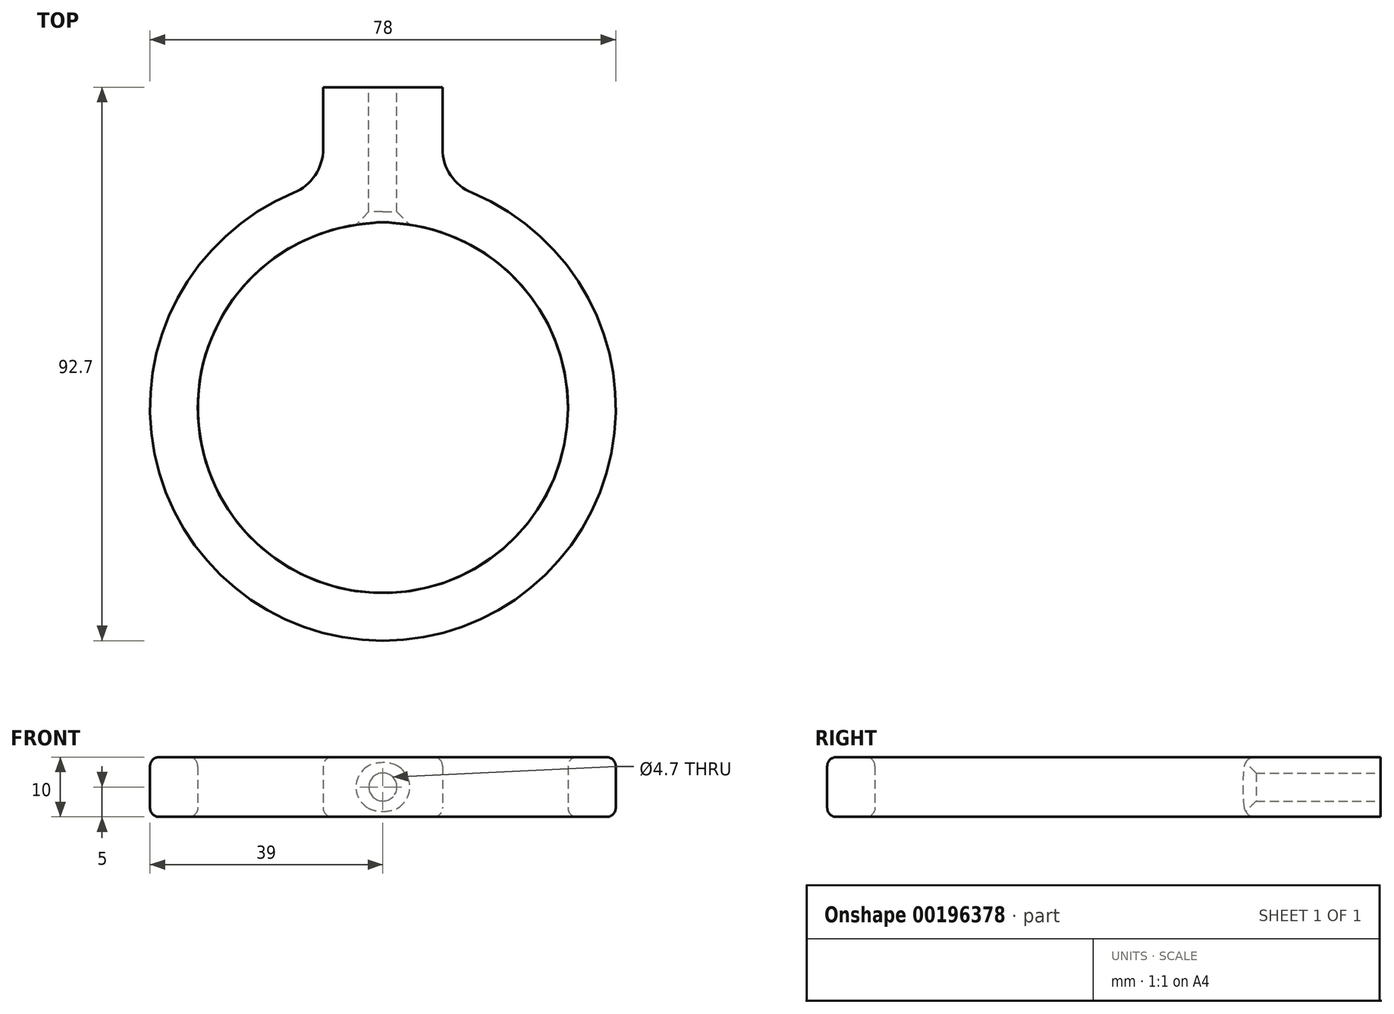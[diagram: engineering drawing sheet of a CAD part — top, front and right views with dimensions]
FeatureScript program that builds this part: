
annotation { "Feature Type Name" : "Feature", "Feature Type Description" : "" }
export const myFeature = defineFeature(function(context is Context, id is Id, definition is map)
    precondition{}
    {
        {
            var Q0;
            Q0=qCreatedBy(makeId("Top.planeOp"),FACE);
            var sketch = newSketch(context, id + "F0", { "sketchPlane" : qUnion([Q0])});
            skCircle(sketch, "E0", {"center": v(0, 0) * mm, "radius": 31 * mm});
            skArc(sketch, "E1.0", {"start": v(-14.94, 36.03) * mm, "mid": v(0, -39) * mm, "end": v(14.94, 36.03) * mm});
            skLineSegment(sketch, "E2.top", {"start": v(-10, 53.7) * mm, "end": v(10, 53.7) * mm});
            skLineSegment(sketch, "E2.left", {"start": v(-10, 43.42) * mm, "end": v(-10, 53.7) * mm});
            skLineSegment(sketch, "E2.right", {"start": v(10, 43.42) * mm, "end": v(10, 53.7) * mm});
            skPoint(sketch, "E2.middle", {"position": v(0, 45.7) * mm});
            skPoint(sketch, "E3.visualSharp", {"position": v(-10, 37.7) * mm});
            skArc(sketch, "E3.filletArc", {"start": v(-14.94, 36.03) * mm, "mid": v(-11.35, 38.97) * mm, "end": v(-10, 43.42) * mm});
            skPoint(sketch, "E4.visualSharp", {"position": v(10, 37.7) * mm});
            skArc(sketch, "E4.filletArc", {"start": v(10, 43.42) * mm, "mid": v(11.35, 38.97) * mm, "end": v(14.94, 36.03) * mm});
            skSolve(sketch);
        }
        {
            var Q0;
            Q0=makeQuery(id+"F0.imprint","IMPRINT",FACE,{"disambiguationData":[TD([[makeQuery(id+"F0.imprint","IMPRINT",EDGE,{"derivedFrom":sQuery(id+"F0.wireOp",EDGE,"E0")}),-1.0]])]});
            extrude(context, id + "F1", {"entities" : qUnion([Q0]), "depth" : 10 * mm});
        }
        {
            var Q0;
            Q0=makeQuery(id+"F1.opExtrude","SWEPT_FACE",FACE,{"disambiguationData":[OSD([sQuery(id+"F0.wireOp",EDGE,"E2.top")])]});
            var sketch = newSketch(context, id + "F2", { "sketchPlane" : qUnion([Q0])});
            skCircle(sketch, "E5", {"center": v(0, 5) * mm, "radius": 2.35 * mm});
            skSolve(sketch);
        }
        {
            var Q0;
            Q0 = qSketchRegion(id + "F2", true);
            extrude(context, id + "F3", {"entities" : qUnion([Q0]), "operationType" : NewBodyOperationType.REMOVE, "endBound" : BoundingType.UP_TO_NEXT, "oppositeDirection" : true, "depth" : 25 * mm});
        }
        {
            var Q0;
            Q0=qCreatedBy(makeId("Right.planeOp"),FACE);
            var sketch = newSketch(context, id + "F4", { "sketchPlane" : qUnion([Q0])});
            skLineSegment(sketch, "E6", {"start": v(30.2, 10) * mm, "end": v(35.2, 5) * mm});
            skLineSegment(sketch, "E7", {"start": v(35.2, 5) * mm, "end": v(30.2, 5) * mm});
            skLineSegment(sketch, "E8", {"start": v(30.2, 5) * mm, "end": v(30.2, 10) * mm});
            skSolve(sketch);
        }
        {
            var Q0;
            Q0 = qSketchRegion(id + "F4", true);
            var Q1;
            Q1=sQuery(id+"F4.wireOp",EDGE,"E7");
            revolve(context, id + "F5", {"operationType" : NewBodyOperationType.REMOVE, "entities" : qUnion([Q0]), "axis" : qUnion([Q1]), "revolveType" : RevolveType.FULL, "oppositeDirection" : true});
        }
        {
            var Q0;
            Q0=makeQuery(id+"F1.opExtrude","CAP_EDGE",EDGE,{"disambiguationData":[OSD([sQuery(id+"F0.wireOp",EDGE,"E1.0")])],"isStart":false});
            var Q1;
            Q1=makeQuery(id+"F1.opExtrude","CAP_EDGE",EDGE,{"disambiguationData":[OSD([sQuery(id+"F0.wireOp",EDGE,"E1.0")])],"isStart":true});
            var Q2;
            Q2=makeQuery(id+"F1.opExtrude","CAP_EDGE",EDGE,{"disambiguationData":[OSD([sQuery(id+"F0.wireOp",EDGE,"E0")])],"isStart":true});
            var Q3;
            Q3=makeQuery(id+"F1.opExtrude","CAP_EDGE",EDGE,{"disambiguationData":[OSD([sQuery(id+"F0.wireOp",EDGE,"E0")])],"isStart":false});
            fillet(context, id + "F6", {"entities" : qUnion([Q0, Q1, Q2, Q3]), "radius" : 1.5 * mm, "tangentPropagation" : true, "allowEdgeOverflow" : false});
        }
    });
